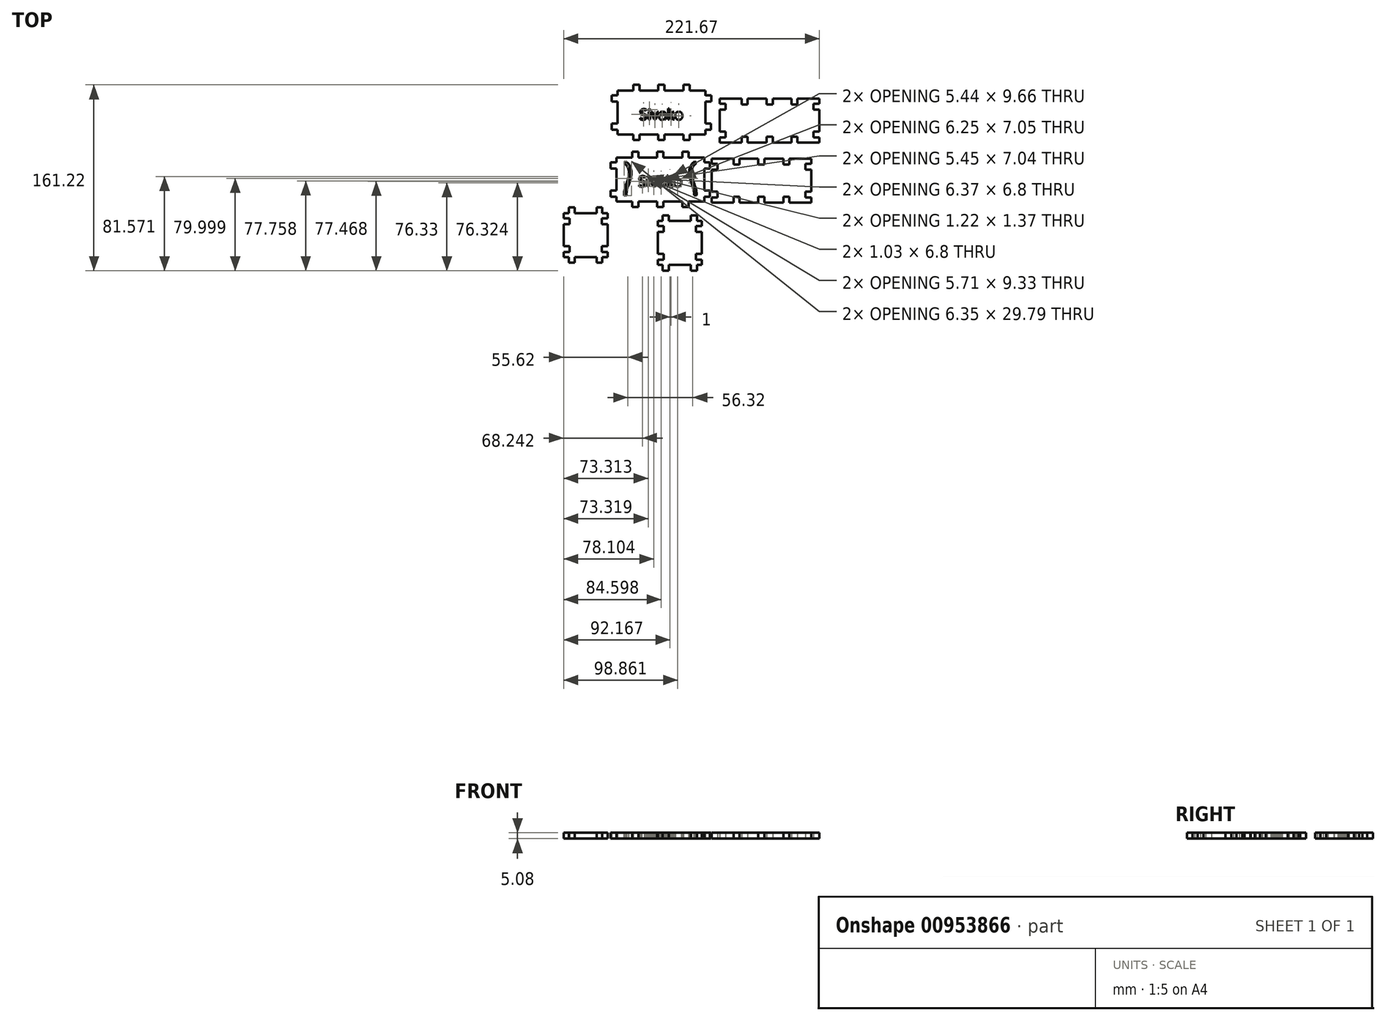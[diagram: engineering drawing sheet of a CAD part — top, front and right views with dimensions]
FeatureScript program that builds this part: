
annotation { "Feature Type Name" : "Feature", "Feature Type Description" : "" }
export const myFeature = defineFeature(function(context is Context, id is Id, definition is map)
    precondition{}
    {
        {
            var Q0;
            Q0=qCreatedBy(makeId("Top.planeOp"),FACE);
            var sketch = newSketch(context, id + "F0", { "sketchPlane" : qUnion([Q0])});
            skLineSegment(sketch, "E0.top", {"start": v(-38.1, -19.05) * mm, "end": v(38.1, -19.05) * mm});
            skLineSegment(sketch, "E0.right", {"start": v(38.1, 19.05) * mm, "end": v(38.1, -19.05) * mm});
            skPoint(sketch, "E0.middle", {"position": v(0, 0) * mm});
            skLineSegment(sketch, "E1", {"start": v(-38.1, 19.05) * mm, "end": v(-38.1, 0) * mm});
            skLineSegment(sketch, "E2", {"start": v(-38.1, 0) * mm, "end": v(-38.1, -19.05) * mm});
            skLineSegment(sketch, "E3", {"start": v(0, 19.05) * mm, "end": v(38.1, 19.05) * mm});
            skLineSegment(sketch, "E4", {"start": v(38.1, 9.52) * mm, "end": v(38.1, 9.52) * mm});
            skLineSegment(sketch, "E5.MirrorCS", {"start": v(38.1, -19.05) * mm, "end": v(38.1, 19.05) * mm});
            skLineSegment(sketch, "E6", {"start": v(38.1, -9.52) * mm, "end": v(38.1, -9.52) * mm});
            skLineSegment(sketch, "E7", {"start": v(38.1, -14.61) * mm, "end": v(38.1, -14.61) * mm});
            skLineSegment(sketch, "E8", {"start": v(-38.1, -14.61) * mm, "end": v(-38.1, -14.61) * mm});
            skLineSegment(sketch, "E9", {"start": v(-38.1, -9.52) * mm, "end": v(-38.1, -9.52) * mm});
            skLineSegment(sketch, "E10", {"start": v(-38.23, 9.65) * mm, "end": v(-38.23, 9.65) * mm});
            skLineSegment(sketch, "E11", {"start": v(-38.1, 9.53) * mm, "end": v(-43.05, 9.53) * mm});
            skLineSegment(sketch, "E12", {"start": v(-43.05, 9.53) * mm, "end": v(-43.05, 14.93) * mm});
            skLineSegment(sketch, "E13", {"start": v(-43.05, 14.93) * mm, "end": v(-38.1, 14.93) * mm});
            skLineSegment(sketch, "E14.MirrorCS", {"start": v(-38.1, -9.52) * mm, "end": v(-43.05, -9.52) * mm});
            skLineSegment(sketch, "E15.MirrorCS", {"start": v(-43.05, -9.52) * mm, "end": v(-43.05, -14.92) * mm});
            skLineSegment(sketch, "E16.MirrorCS", {"start": v(-43.05, -14.92) * mm, "end": v(-38.1, -14.92) * mm});
            skLineSegment(sketch, "E17", {"start": v(-38.1, -14.92) * mm, "end": v(-38.1, -14.92) * mm});
            skLineSegment(sketch, "E18.MirrorCS", {"start": v(43.05, 9.52) * mm, "end": v(43.05, 14.92) * mm});
            skLineSegment(sketch, "E19.MirrorCS", {"start": v(43.05, 14.92) * mm, "end": v(38.1, 14.92) * mm});
            skLineSegment(sketch, "E20.MirrorCS", {"start": v(38.1, 9.52) * mm, "end": v(43.05, 9.52) * mm});
            skLineSegment(sketch, "E21.MirrorCS", {"start": v(38.1, -9.52) * mm, "end": v(43.05, -9.52) * mm});
            skLineSegment(sketch, "E22.MirrorCS", {"start": v(43.05, -14.92) * mm, "end": v(38.1, -14.92) * mm});
            skLineSegment(sketch, "E23.MirrorCS", {"start": v(43.05, -9.52) * mm, "end": v(43.05, -14.92) * mm});
            skLineSegment(sketch, "E24", {"start": v(-19.05, 19.05) * mm, "end": v(-19.05, 24) * mm});
            skLineSegment(sketch, "E25", {"start": v(-19.05, 24) * mm, "end": v(-24.45, 24) * mm});
            skLineSegment(sketch, "E26", {"start": v(-24.45, 24) * mm, "end": v(-24.45, 19.05) * mm});
            skLineSegment(sketch, "E27.MirrorCS", {"start": v(19.05, 19.05) * mm, "end": v(19.05, 24) * mm});
            skLineSegment(sketch, "E28.MirrorCS", {"start": v(19.05, 24) * mm, "end": v(24.45, 24) * mm});
            skLineSegment(sketch, "E29.MirrorCS", {"start": v(24.45, 24) * mm, "end": v(24.45, 19.05) * mm});
            skLineSegment(sketch, "E30.MirrorCS", {"start": v(-19.05, -19.05) * mm, "end": v(-19.05, -24) * mm});
            skLineSegment(sketch, "E31.MirrorCS", {"start": v(-24.45, -24) * mm, "end": v(-24.45, -19.05) * mm});
            skLineSegment(sketch, "E32.MirrorCS", {"start": v(-19.05, -24) * mm, "end": v(-24.45, -24) * mm});
            skLineSegment(sketch, "E33.MirrorCS", {"start": v(19.05, -19.05) * mm, "end": v(19.05, -24) * mm});
            skLineSegment(sketch, "E34.MirrorCS", {"start": v(19.05, -24) * mm, "end": v(24.45, -24) * mm});
            skLineSegment(sketch, "E35.MirrorCS", {"start": v(24.45, -24) * mm, "end": v(24.45, -19.05) * mm});
            skText(sketch, "E36", { "text": "Sivako", "fontName": "OpenSans-Regular.ttf"});
            skPoint(sketch, "E36.firstSnap0", {"position": v(-19.05, 9.53) * mm});
            skPoint(sketch, "E36.secondSnap0", {"position": v(19.05, -9.52) * mm});
            skLineSegment(sketch, "E37.top", {"start": v(-37.1, 39.01) * mm, "end": v(39.1, 39.01) * mm});
            skLineSegment(sketch, "E37.right", {"start": v(39.1, 77.11) * mm, "end": v(39.1, 39.01) * mm});
            skPoint(sketch, "E37.middle", {"position": v(1, 58.06) * mm});
            skLineSegment(sketch, "E38", {"start": v(-37.1, 77.11) * mm, "end": v(-37.1, 58.07) * mm});
            skLineSegment(sketch, "E39", {"start": v(-37.1, 58.07) * mm, "end": v(-37.1, 39.01) * mm});
            skLineSegment(sketch, "E40", {"start": v(-37.1, 77.11) * mm, "end": v(1, 77.11) * mm});
            skLineSegment(sketch, "E41", {"start": v(1, 77.11) * mm, "end": v(39.1, 77.11) * mm});
            skLineSegment(sketch, "E42", {"start": v(39.1, 72.68) * mm, "end": v(39.1, 72.68) * mm});
            skLineSegment(sketch, "E43", {"start": v(39.1, 67.59) * mm, "end": v(39.1, 67.59) * mm});
            skLineSegment(sketch, "E44.MirrorCS", {"start": v(39.1, 39.01) * mm, "end": v(39.1, 77.11) * mm});
            skLineSegment(sketch, "E45", {"start": v(39.1, 48.54) * mm, "end": v(39.1, 48.54) * mm});
            skLineSegment(sketch, "E46", {"start": v(39.1, 43.45) * mm, "end": v(39.1, 43.45) * mm});
            skLineSegment(sketch, "E47", {"start": v(-37.1, 43.45) * mm, "end": v(-37.1, 43.45) * mm});
            skLineSegment(sketch, "E48", {"start": v(-37.1, 48.54) * mm, "end": v(-37.1, 48.54) * mm});
            skLineSegment(sketch, "E49", {"start": v(-37.23, 67.72) * mm, "end": v(-37.23, 67.72) * mm});
            skLineSegment(sketch, "E50", {"start": v(-37.1, 67.59) * mm, "end": v(-42.05, 67.59) * mm});
            skLineSegment(sketch, "E51", {"start": v(-42.05, 67.59) * mm, "end": v(-42.05, 72.99) * mm});
            skLineSegment(sketch, "E52", {"start": v(-42.05, 72.99) * mm, "end": v(-37.1, 72.99) * mm});
            skLineSegment(sketch, "E53.MirrorCS", {"start": v(-37.1, 48.54) * mm, "end": v(-42.06, 48.54) * mm});
            skLineSegment(sketch, "E54.MirrorCS", {"start": v(-42.06, 48.54) * mm, "end": v(-42.06, 43.14) * mm});
            skLineSegment(sketch, "E55.MirrorCS", {"start": v(-42.06, 43.14) * mm, "end": v(-37.1, 43.14) * mm});
            skLineSegment(sketch, "E56", {"start": v(-37.1, 43.14) * mm, "end": v(-37.1, 43.14) * mm});
            skLineSegment(sketch, "E57.MirrorCS", {"start": v(44.05, 67.59) * mm, "end": v(44.05, 72.99) * mm});
            skLineSegment(sketch, "E58.MirrorCS", {"start": v(44.05, 72.99) * mm, "end": v(39.1, 72.99) * mm});
            skLineSegment(sketch, "E59.MirrorCS", {"start": v(39.1, 67.59) * mm, "end": v(44.05, 67.59) * mm});
            skLineSegment(sketch, "E60.MirrorCS", {"start": v(39.1, 48.54) * mm, "end": v(44.05, 48.54) * mm});
            skLineSegment(sketch, "E61.MirrorCS", {"start": v(44.05, 43.14) * mm, "end": v(39.1, 43.14) * mm});
            skLineSegment(sketch, "E62.MirrorCS", {"start": v(44.05, 48.54) * mm, "end": v(44.05, 43.14) * mm});
            skLineSegment(sketch, "E63", {"start": v(-18.05, 77.11) * mm, "end": v(-18.05, 82.07) * mm});
            skLineSegment(sketch, "E64", {"start": v(-18.05, 82.07) * mm, "end": v(-23.45, 82.07) * mm});
            skLineSegment(sketch, "E65", {"start": v(-23.45, 82.07) * mm, "end": v(-23.45, 77.11) * mm});
            skLineSegment(sketch, "E66.MirrorCS", {"start": v(20.05, 77.11) * mm, "end": v(20.05, 82.06) * mm});
            skLineSegment(sketch, "E67.MirrorCS", {"start": v(20.05, 82.06) * mm, "end": v(25.45, 82.06) * mm});
            skLineSegment(sketch, "E68.MirrorCS", {"start": v(25.45, 82.06) * mm, "end": v(25.45, 77.11) * mm});
            skLineSegment(sketch, "E69.MirrorCS", {"start": v(-18.05, 39.02) * mm, "end": v(-18.05, 34.06) * mm});
            skLineSegment(sketch, "E70.MirrorCS", {"start": v(-23.45, 34.06) * mm, "end": v(-23.45, 39.02) * mm});
            skLineSegment(sketch, "E71.MirrorCS", {"start": v(-18.05, 34.06) * mm, "end": v(-23.45, 34.06) * mm});
            skLineSegment(sketch, "E72.MirrorCS", {"start": v(20.05, 39.02) * mm, "end": v(20.05, 34.06) * mm});
            skLineSegment(sketch, "E73.MirrorCS", {"start": v(20.05, 34.06) * mm, "end": v(25.45, 34.06) * mm});
            skLineSegment(sketch, "E74.MirrorCS", {"start": v(25.45, 34.06) * mm, "end": v(25.45, 39.02) * mm});
            skText(sketch, "E75", { "text": "Sivako", "fontName": "OpenSans-Regular.ttf"});
            skPoint(sketch, "E75.firstSnap0", {"position": v(-18.05, 67.59) * mm});
            skPoint(sketch, "E75.secondSnap0", {"position": v(20.05, 48.54) * mm});
            skLineSegment(sketch, "E76", {"start": v(0, 19.05) * mm, "end": v(-2.7, 19.05) * mm});
            skLineSegment(sketch, "E77", {"start": v(-2.7, 19.05) * mm, "end": v(2.7, 19.05) * mm});
            skLineSegment(sketch, "E78", {"start": v(2.7, 19.05) * mm, "end": v(2.7, 24) * mm});
            skLineSegment(sketch, "E79", {"start": v(2.7, 24) * mm, "end": v(-2.7, 24) * mm});
            skLineSegment(sketch, "E80", {"start": v(-2.7, 24) * mm, "end": v(-2.7, 19.05) * mm});
            skLineSegment(sketch, "E81.MirrorCS", {"start": v(-2.7, -24) * mm, "end": v(-2.7, -19.05) * mm});
            skLineSegment(sketch, "E82.MirrorCS", {"start": v(2.7, -24) * mm, "end": v(-2.7, -24) * mm});
            skLineSegment(sketch, "E83.MirrorCS", {"start": v(2.7, -19.05) * mm, "end": v(2.7, -24) * mm});
            skLineSegment(sketch, "E84", {"start": v(1, 39.01) * mm, "end": v(-1.7, 39.01) * mm});
            skLineSegment(sketch, "E85", {"start": v(1, 39.01) * mm, "end": v(3.7, 39.01) * mm});
            skLineSegment(sketch, "E86", {"start": v(3.7, 39.01) * mm, "end": v(3.7, 34.06) * mm});
            skLineSegment(sketch, "E87", {"start": v(3.7, 34.06) * mm, "end": v(-1.7, 34.06) * mm});
            skLineSegment(sketch, "E88", {"start": v(-1.7, 34.06) * mm, "end": v(-1.7, 39.01) * mm});
            skLineSegment(sketch, "E89.MirrorCS", {"start": v(3.7, 77.12) * mm, "end": v(3.7, 82.07) * mm});
            skLineSegment(sketch, "E90.MirrorCS", {"start": v(3.7, 82.07) * mm, "end": v(-1.7, 82.07) * mm});
            skLineSegment(sketch, "E91.MirrorCS", {"start": v(-1.7, 82.07) * mm, "end": v(-1.7, 77.12) * mm});
            skLineSegment(sketch, "E92", {"start": v(-1.7, 77.12) * mm, "end": v(-1.7, 77.11) * mm});
            skLineSegment(sketch, "E93", {"start": v(3.7, 77.12) * mm, "end": v(3.7, 77.11) * mm});
            skLineSegment(sketch, "E94", {"start": v(0, 2.94) * mm, "end": v(0, 19.05) * mm, "construction": true});
            skLineSegment(sketch, "E95.MirrorCS", {"start": v(28.77, -19.05) * mm, "end": v(28.77, -19.05) * mm});
            skLineSegment(sketch, "E96", {"start": v(-24.45, 19.05) * mm, "end": v(-38.1, 19.05) * mm});
            skLineSegment(sketch, "E97", {"start": v(-20, 19.05) * mm, "end": v(-2.7, 19.05) * mm});
            skLineSegment(sketch, "E98.MirrorCS", {"start": v(31.28, 19.05) * mm, "end": v(31.28, 14.05) * mm});
            skFitSpline(sketch, "E99", {"points": [v(-31.27, 14.05) * mm, v(-31.28, -14.04) * mm], "startDerivative": vector(30.27, -22.26) * mm, "endDerivative": vector(4.94, -25.33) * mm});
            skFitSpline(sketch, "E100.0", {"points": [v(-30.03, 15.74) * mm, v(-29.3, 15.2) * mm, v(-28.02, 14.07) * mm, v(-26.57, 12.18) * mm, v(-25.61, 10.13) * mm, v(-25.1, 8.02) * mm, v(-24.99, 5.92) * mm, v(-25.22, 3.15) * mm, v(-26.03, -0.23) * mm, v(-27.36, -4.12) * mm, v(-28.4, -7.17) * mm, v(-29, -9.43) * mm, v(-29.28, -11) * mm, v(-29.37, -12.42) * mm, v(-29.29, -13.25) * mm, v(-29.21, -13.64) * mm]});
            skLineSegment(sketch, "E101", {"start": v(-31.28, -14.04) * mm, "end": v(-29.21, -13.64) * mm});
            skLineSegment(sketch, "E102", {"start": v(-31.27, 14.05) * mm, "end": v(-30.03, 15.74) * mm});
            skPoint(sketch, "E103.start.orphan", {"position": v(-31.27, 19.05) * mm});
            skPoint(sketch, "E104.MirrorCS.start.orphan", {"position": v(-31.28, -19.04) * mm});
            skPoint(sketch, "E105.end.orphan", {"position": v(-28.77, -19.05) * mm});
            skPoint(sketch, "E105.start.orphan", {"position": v(-29.46, -18.35) * mm});
            skPoint(sketch, "E106.MirrorCS.end.orphan", {"position": v(31.28, -14.04) * mm});
            skPoint(sketch, "E106.MirrorCS.start.orphan", {"position": v(31.28, -19.04) * mm});
            skPoint(sketch, "E107.orphan", {"position": v(29.46, -18.35) * mm});
            skPoint(sketch, "E108.MirrorCS.end.orphan", {"position": v(31.28, 14.05) * mm});
            skPoint(sketch, "E108.MirrorCS.start.orphan", {"position": v(31.28, 19.05) * mm});
            skFitSpline(sketch, "E109.MirrorCS", {"points": [v(31.28, 14.05) * mm, v(31.27, -14.05) * mm], "startDerivative": vector(-30.27, -22.26) * mm, "endDerivative": vector(-4.94, -25.33) * mm});
            skFitSpline(sketch, "E110.0", {"points": [v(30.03, 15.74) * mm, v(29.3, 15.2) * mm, v(28.02, 14.07) * mm, v(26.57, 12.17) * mm, v(25.61, 10.13) * mm, v(25.1, 8.02) * mm, v(24.99, 5.91) * mm, v(25.22, 3.14) * mm, v(26.03, -0.23) * mm, v(27.36, -4.12) * mm, v(28.4, -7.18) * mm, v(29, -9.43) * mm, v(29.28, -11) * mm, v(29.37, -12.42) * mm, v(29.29, -13.26) * mm, v(29.21, -13.65) * mm]});
            skLineSegment(sketch, "E111.MirrorCS", {"start": v(31.27, -14.05) * mm, "end": v(29.21, -13.65) * mm});
            skLineSegment(sketch, "E112.MirrorCS", {"start": v(31.28, 14.05) * mm, "end": v(30.03, 15.74) * mm});
            skLineSegment(sketch, "E113", {"start": v(38.1, 14.92) * mm, "end": v(38.1, 14.92) * mm});
            const initialGuessF0  = {"E36": [-0.01905, -0.00622, 1, 0, 0.00915], "E75": [-0.01805, 0.05184, 1, 0, 0.00915]};
            skSetInitialGuess(sketch, initialGuessF0);
            skSolve(sketch);
        }
        {
            var Q0;
            Q0=qSketchRegion(id+"F0",true);
            var Q1;
            {var subQ6=sQuery(id+"F0.wireOp",EDGE,"E0.top");Q1=makeQuery(id+"F0.imprint","IMPRINT",FACE,{"disambiguationData":[TD([[makeQuery(id+"F0.imprint","IMPRINT",EDGE,{"derivedFrom":subQ6}),1.0]])]});}
            var Q2;
            {var subQ0=sQuery(id+"F0.wireOp",EDGE,"E36.sketch_text.stroke-40");Q2=makeQuery(id+"F0.imprint","IMPRINT",FACE,{"disambiguationData":[TD([[makeQuery(id+"F0.imprint","IMPRINT",EDGE,{"derivedFrom":subQ0}),1.0]])]});}
            var Q3;
            {var subQ0=sQuery(id+"F0.wireOp",EDGE,"E36.sketch_text.stroke-54");Q3=makeQuery(id+"F0.imprint","IMPRINT",FACE,{"disambiguationData":[TD([[makeQuery(id+"F0.imprint","IMPRINT",EDGE,{"derivedFrom":subQ0}),1.0]])]});}
            extrude(context, id + "F1", {"entities" : qUnion([Q0, Q1, Q2, Q3]), "depth" : 5.08 * mm, "offsetDistance" : 25.4 * mm});
        }
        {
            var Q0;
            Q0=qCreatedBy(makeId("Top.planeOp"),FACE);
            var sketch = newSketch(context, id + "F2", { "sketchPlane" : qUnion([Q0])});
            skLineSegment(sketch, "E114.top", {"start": v(-83.78, -67.33) * mm, "end": v(-45.68, -67.33) * mm});
            skLineSegment(sketch, "E114.right", {"start": v(-45.68, -29.23) * mm, "end": v(-45.68, -67.33) * mm});
            skPoint(sketch, "E114.middle", {"position": v(-64.73, -48.28) * mm});
            skLineSegment(sketch, "E115", {"start": v(-83.78, -29.23) * mm, "end": v(-83.78, -48.28) * mm});
            skLineSegment(sketch, "E116", {"start": v(-83.78, -48.28) * mm, "end": v(-83.78, -67.33) * mm});
            skLineSegment(sketch, "E117", {"start": v(-83.78, -38.75) * mm, "end": v(-78.7, -38.75) * mm});
            skLineSegment(sketch, "E118", {"start": v(-78.7, -38.75) * mm, "end": v(-78.7, -33.67) * mm});
            skLineSegment(sketch, "E119", {"start": v(-78.7, -33.67) * mm, "end": v(-83.78, -33.67) * mm});
            skLineSegment(sketch, "E120.MirrorCS", {"start": v(-83.78, -57.8) * mm, "end": v(-78.7, -57.8) * mm});
            skLineSegment(sketch, "E121.MirrorCS", {"start": v(-78.7, -57.8) * mm, "end": v(-78.7, -62.88) * mm});
            skLineSegment(sketch, "E122.MirrorCS", {"start": v(-78.7, -62.88) * mm, "end": v(-83.78, -62.88) * mm});
            skLineSegment(sketch, "E123.MirrorCS", {"start": v(-50.76, -38.75) * mm, "end": v(-50.76, -33.67) * mm});
            skLineSegment(sketch, "E124.MirrorCS", {"start": v(-50.76, -33.67) * mm, "end": v(-45.68, -33.67) * mm});
            skLineSegment(sketch, "E125.MirrorCS", {"start": v(-45.68, -38.75) * mm, "end": v(-50.76, -38.75) * mm});
            skLineSegment(sketch, "E126.MirrorCS", {"start": v(-45.68, -57.8) * mm, "end": v(-50.76, -57.8) * mm});
            skLineSegment(sketch, "E127.MirrorCS", {"start": v(-50.76, -57.8) * mm, "end": v(-50.76, -62.88) * mm});
            skLineSegment(sketch, "E128.MirrorCS", {"start": v(-50.76, -62.88) * mm, "end": v(-45.68, -62.88) * mm});
            skLineSegment(sketch, "E129", {"start": v(-83.78, -29.23) * mm, "end": v(-64.73, -29.23) * mm});
            skLineSegment(sketch, "E130", {"start": v(-64.73, -29.23) * mm, "end": v(-45.68, -29.23) * mm});
            skLineSegment(sketch, "E131", {"start": v(-74.25, -29.23) * mm, "end": v(-74.25, -24.28) * mm});
            skLineSegment(sketch, "E132", {"start": v(-74.25, -24.28) * mm, "end": v(-79.2, -24.28) * mm});
            skLineSegment(sketch, "E133", {"start": v(-79.2, -24.28) * mm, "end": v(-79.2, -29.23) * mm});
            skLineSegment(sketch, "E134", {"start": v(-55.2, -29.23) * mm, "end": v(-55.2, -24.28) * mm});
            skLineSegment(sketch, "E135", {"start": v(-55.2, -24.28) * mm, "end": v(-50.25, -24.28) * mm});
            skLineSegment(sketch, "E136", {"start": v(-50.25, -24.28) * mm, "end": v(-50.25, -29.23) * mm});
            skLineSegment(sketch, "E137.MirrorCS", {"start": v(-74.25, -67.33) * mm, "end": v(-74.25, -72.28) * mm});
            skLineSegment(sketch, "E138.MirrorCS", {"start": v(-74.25, -72.28) * mm, "end": v(-79.2, -72.28) * mm});
            skLineSegment(sketch, "E139.MirrorCS", {"start": v(-79.2, -72.28) * mm, "end": v(-79.2, -67.33) * mm});
            skLineSegment(sketch, "E140.MirrorCS", {"start": v(-55.2, -67.33) * mm, "end": v(-55.2, -72.28) * mm});
            skLineSegment(sketch, "E141.MirrorCS", {"start": v(-55.2, -72.28) * mm, "end": v(-50.25, -72.28) * mm});
            skLineSegment(sketch, "E142.MirrorCS", {"start": v(-50.25, -72.28) * mm, "end": v(-50.25, -67.33) * mm});
            skLineSegment(sketch, "E143.top", {"start": v(-2.2, -74.2) * mm, "end": v(35.9, -74.2) * mm});
            skLineSegment(sketch, "E143.right", {"start": v(35.9, -36.1) * mm, "end": v(35.9, -74.2) * mm});
            skPoint(sketch, "E143.middle", {"position": v(16.85, -55.15) * mm});
            skLineSegment(sketch, "E144", {"start": v(-2.2, -36.1) * mm, "end": v(-2.2, -55.15) * mm});
            skLineSegment(sketch, "E145", {"start": v(-2.2, -55.15) * mm, "end": v(-2.2, -74.2) * mm});
            skLineSegment(sketch, "E146", {"start": v(-2.2, -45.62) * mm, "end": v(2.88, -45.62) * mm});
            skLineSegment(sketch, "E147", {"start": v(2.88, -45.62) * mm, "end": v(2.88, -40.54) * mm});
            skLineSegment(sketch, "E148", {"start": v(2.88, -40.54) * mm, "end": v(-2.2, -40.54) * mm});
            skLineSegment(sketch, "E149.MirrorCS", {"start": v(-2.2, -64.67) * mm, "end": v(2.88, -64.67) * mm});
            skLineSegment(sketch, "E150.MirrorCS", {"start": v(2.88, -64.67) * mm, "end": v(2.88, -69.75) * mm});
            skLineSegment(sketch, "E151.MirrorCS", {"start": v(2.88, -69.75) * mm, "end": v(-2.2, -69.75) * mm});
            skLineSegment(sketch, "E152.MirrorCS", {"start": v(30.82, -45.62) * mm, "end": v(30.82, -40.54) * mm});
            skLineSegment(sketch, "E153.MirrorCS", {"start": v(30.82, -40.54) * mm, "end": v(35.9, -40.54) * mm});
            skLineSegment(sketch, "E154.MirrorCS", {"start": v(35.9, -45.62) * mm, "end": v(30.82, -45.62) * mm});
            skLineSegment(sketch, "E155.MirrorCS", {"start": v(35.9, -64.67) * mm, "end": v(30.82, -64.67) * mm});
            skLineSegment(sketch, "E156.MirrorCS", {"start": v(30.82, -64.67) * mm, "end": v(30.82, -69.75) * mm});
            skLineSegment(sketch, "E157.MirrorCS", {"start": v(30.82, -69.75) * mm, "end": v(35.9, -69.75) * mm});
            skLineSegment(sketch, "E158", {"start": v(-2.2, -36.1) * mm, "end": v(16.85, -36.1) * mm});
            skLineSegment(sketch, "E159", {"start": v(16.85, -36.1) * mm, "end": v(35.9, -36.1) * mm});
            skLineSegment(sketch, "E160", {"start": v(7.33, -36.1) * mm, "end": v(7.33, -31.14) * mm});
            skLineSegment(sketch, "E161", {"start": v(7.33, -31.14) * mm, "end": v(1.93, -31.14) * mm});
            skLineSegment(sketch, "E162", {"start": v(1.93, -31.14) * mm, "end": v(1.93, -36.1) * mm});
            skLineSegment(sketch, "E163", {"start": v(26.38, -36.1) * mm, "end": v(26.38, -31.14) * mm});
            skLineSegment(sketch, "E164", {"start": v(26.38, -31.14) * mm, "end": v(31.78, -31.14) * mm});
            skLineSegment(sketch, "E165", {"start": v(31.78, -31.14) * mm, "end": v(31.78, -36.1) * mm});
            skLineSegment(sketch, "E166.MirrorCS", {"start": v(7.33, -74.2) * mm, "end": v(7.33, -79.15) * mm});
            skLineSegment(sketch, "E167.MirrorCS", {"start": v(7.33, -79.15) * mm, "end": v(1.93, -79.15) * mm});
            skLineSegment(sketch, "E168.MirrorCS", {"start": v(1.93, -79.15) * mm, "end": v(1.93, -74.2) * mm});
            skLineSegment(sketch, "E169.MirrorCS", {"start": v(26.38, -74.2) * mm, "end": v(26.38, -79.15) * mm});
            skLineSegment(sketch, "E170.MirrorCS", {"start": v(26.38, -79.15) * mm, "end": v(31.78, -79.15) * mm});
            skLineSegment(sketch, "E171.MirrorCS", {"start": v(31.78, -79.15) * mm, "end": v(31.78, -74.2) * mm});
            skLineSegment(sketch, "E172.top", {"start": v(44.41, -20.23) * mm, "end": v(130.77, -20.23) * mm});
            skLineSegment(sketch, "E172.right", {"start": v(130.77, 17.87) * mm, "end": v(130.77, -20.23) * mm});
            skPoint(sketch, "E172.middle", {"position": v(87.6, -1.18) * mm});
            skLineSegment(sketch, "E173", {"start": v(44.41, 17.87) * mm, "end": v(44.41, -1.18) * mm});
            skLineSegment(sketch, "E174", {"start": v(44.41, -1.18) * mm, "end": v(44.41, -20.23) * mm});
            skLineSegment(sketch, "E175", {"start": v(44.41, 17.87) * mm, "end": v(87.6, 17.87) * mm});
            skLineSegment(sketch, "E176", {"start": v(87.6, 17.87) * mm, "end": v(130.77, 17.87) * mm});
            skLineSegment(sketch, "E177", {"start": v(87.6, 17.87) * mm, "end": v(49.5, 17.87) * mm});
            skLineSegment(sketch, "E178", {"start": v(87.6, 17.87) * mm, "end": v(125.7, 17.87) * mm});
            skLineSegment(sketch, "E179", {"start": v(68.54, 17.87) * mm, "end": v(68.54, 12.8) * mm});
            skLineSegment(sketch, "E180", {"start": v(68.54, 12.8) * mm, "end": v(63.46, 12.8) * mm});
            skLineSegment(sketch, "E181", {"start": v(63.46, 12.8) * mm, "end": v(63.46, 17.87) * mm});
            skLineSegment(sketch, "E182.MirrorCS", {"start": v(106.64, 17.87) * mm, "end": v(106.64, 12.8) * mm});
            skLineSegment(sketch, "E183.MirrorCS", {"start": v(106.64, 12.8) * mm, "end": v(111.72, 12.8) * mm});
            skLineSegment(sketch, "E184.MirrorCS", {"start": v(111.72, 12.8) * mm, "end": v(111.72, 17.87) * mm});
            skLineSegment(sketch, "E185.MirrorCS", {"start": v(68.54, -15.15) * mm, "end": v(63.46, -15.15) * mm});
            skLineSegment(sketch, "E186.MirrorCS", {"start": v(63.46, -15.15) * mm, "end": v(63.46, -20.23) * mm});
            skLineSegment(sketch, "E187.MirrorCS", {"start": v(68.54, -20.23) * mm, "end": v(68.54, -15.15) * mm});
            skLineSegment(sketch, "E188.MirrorCS", {"start": v(106.64, -15.15) * mm, "end": v(111.72, -15.15) * mm});
            skLineSegment(sketch, "E189.MirrorCS", {"start": v(106.64, -20.23) * mm, "end": v(106.64, -15.15) * mm});
            skLineSegment(sketch, "E190.MirrorCS", {"start": v(111.72, -15.15) * mm, "end": v(111.72, -20.23) * mm});
            skLineSegment(sketch, "E191.MirrorCS", {"start": v(49.5, 13.43) * mm, "end": v(44.41, 13.43) * mm});
            skLineSegment(sketch, "E192.MirrorCS", {"start": v(49.5, 8.35) * mm, "end": v(49.5, 13.43) * mm});
            skLineSegment(sketch, "E193.MirrorCS", {"start": v(44.41, 8.35) * mm, "end": v(49.5, 8.35) * mm});
            skLineSegment(sketch, "E194.MirrorCS", {"start": v(49.5, -10.7) * mm, "end": v(49.5, -15.78) * mm});
            skLineSegment(sketch, "E195.MirrorCS", {"start": v(49.5, -15.78) * mm, "end": v(44.41, -15.78) * mm});
            skLineSegment(sketch, "E196.MirrorCS", {"start": v(44.41, -10.7) * mm, "end": v(49.5, -10.7) * mm});
            skLineSegment(sketch, "E197.MirrorCS", {"start": v(125.7, 8.35) * mm, "end": v(125.7, 13.43) * mm});
            skLineSegment(sketch, "E198.MirrorCS", {"start": v(125.7, 13.43) * mm, "end": v(130.77, 13.43) * mm});
            skLineSegment(sketch, "E199.MirrorCS", {"start": v(130.77, 8.35) * mm, "end": v(125.7, 8.35) * mm});
            skLineSegment(sketch, "E200.MirrorCS", {"start": v(130.77, -10.7) * mm, "end": v(125.7, -10.7) * mm});
            skLineSegment(sketch, "E201.MirrorCS", {"start": v(125.7, -10.7) * mm, "end": v(125.7, -15.78) * mm});
            skLineSegment(sketch, "E202.MirrorCS", {"start": v(125.7, -15.78) * mm, "end": v(130.77, -15.78) * mm});
            skLineSegment(sketch, "E203.top", {"start": v(51.53, 32.1) * mm, "end": v(137.89, 32.1) * mm});
            skLineSegment(sketch, "E203.right", {"start": v(137.89, 70.2) * mm, "end": v(137.89, 32.1) * mm});
            skPoint(sketch, "E203.middle", {"position": v(94.7, 51.15) * mm});
            skLineSegment(sketch, "E204", {"start": v(51.53, 70.2) * mm, "end": v(51.53, 51.15) * mm});
            skLineSegment(sketch, "E205", {"start": v(51.53, 51.15) * mm, "end": v(51.53, 32.1) * mm});
            skLineSegment(sketch, "E206", {"start": v(51.53, 70.2) * mm, "end": v(94.7, 70.2) * mm});
            skLineSegment(sketch, "E207", {"start": v(94.7, 70.2) * mm, "end": v(137.89, 70.2) * mm});
            skLineSegment(sketch, "E208", {"start": v(94.7, 70.2) * mm, "end": v(56.6, 70.2) * mm});
            skLineSegment(sketch, "E209", {"start": v(94.7, 70.2) * mm, "end": v(132.8, 70.2) * mm});
            skLineSegment(sketch, "E210", {"start": v(75.66, 70.2) * mm, "end": v(75.66, 65.12) * mm});
            skLineSegment(sketch, "E211", {"start": v(75.66, 65.12) * mm, "end": v(70.58, 65.12) * mm});
            skLineSegment(sketch, "E212", {"start": v(70.58, 65.12) * mm, "end": v(70.58, 70.2) * mm});
            skLineSegment(sketch, "E213.MirrorCS", {"start": v(113.76, 70.2) * mm, "end": v(113.76, 65.12) * mm});
            skLineSegment(sketch, "E214.MirrorCS", {"start": v(113.76, 65.12) * mm, "end": v(118.84, 65.12) * mm});
            skLineSegment(sketch, "E215.MirrorCS", {"start": v(118.84, 65.12) * mm, "end": v(118.84, 70.2) * mm});
            skLineSegment(sketch, "E216.MirrorCS", {"start": v(75.66, 37.18) * mm, "end": v(70.58, 37.18) * mm});
            skLineSegment(sketch, "E217.MirrorCS", {"start": v(70.58, 37.18) * mm, "end": v(70.58, 32.1) * mm});
            skLineSegment(sketch, "E218.MirrorCS", {"start": v(75.66, 32.1) * mm, "end": v(75.66, 37.18) * mm});
            skLineSegment(sketch, "E219.MirrorCS", {"start": v(113.76, 37.18) * mm, "end": v(118.84, 37.18) * mm});
            skLineSegment(sketch, "E220.MirrorCS", {"start": v(113.76, 32.1) * mm, "end": v(113.76, 37.18) * mm});
            skLineSegment(sketch, "E221.MirrorCS", {"start": v(118.84, 37.18) * mm, "end": v(118.84, 32.1) * mm});
            skLineSegment(sketch, "E222.MirrorCS", {"start": v(56.6, 65.76) * mm, "end": v(51.53, 65.76) * mm});
            skLineSegment(sketch, "E223.MirrorCS", {"start": v(56.6, 60.68) * mm, "end": v(56.6, 65.76) * mm});
            skLineSegment(sketch, "E224.MirrorCS", {"start": v(51.53, 60.68) * mm, "end": v(56.6, 60.68) * mm});
            skLineSegment(sketch, "E225.MirrorCS", {"start": v(56.6, 41.63) * mm, "end": v(56.6, 36.55) * mm});
            skLineSegment(sketch, "E226.MirrorCS", {"start": v(56.6, 36.55) * mm, "end": v(51.53, 36.55) * mm});
            skLineSegment(sketch, "E227.MirrorCS", {"start": v(51.53, 41.63) * mm, "end": v(56.6, 41.63) * mm});
            skLineSegment(sketch, "E228.MirrorCS", {"start": v(132.8, 60.68) * mm, "end": v(132.8, 65.76) * mm});
            skLineSegment(sketch, "E229.MirrorCS", {"start": v(132.8, 65.76) * mm, "end": v(137.89, 65.76) * mm});
            skLineSegment(sketch, "E230.MirrorCS", {"start": v(137.89, 60.68) * mm, "end": v(132.8, 60.68) * mm});
            skLineSegment(sketch, "E231.MirrorCS", {"start": v(137.89, 41.63) * mm, "end": v(132.8, 41.63) * mm});
            skLineSegment(sketch, "E232.MirrorCS", {"start": v(132.8, 41.63) * mm, "end": v(132.8, 36.55) * mm});
            skLineSegment(sketch, "E233.MirrorCS", {"start": v(132.8, 36.55) * mm, "end": v(137.89, 36.55) * mm});
            skPoint(sketch, "E234.orphan", {"position": v(130.77, -1.18) * mm});
            skLineSegment(sketch, "E235", {"start": v(87.6, 17.87) * mm, "end": v(84.9, 17.87) * mm});
            skLineSegment(sketch, "E236", {"start": v(84.9, 17.87) * mm, "end": v(90.3, 17.87) * mm});
            skLineSegment(sketch, "E237", {"start": v(90.3, 17.87) * mm, "end": v(90.3, 12.8) * mm});
            skLineSegment(sketch, "E238", {"start": v(90.3, 12.8) * mm, "end": v(84.9, 12.8) * mm});
            skLineSegment(sketch, "E239", {"start": v(84.9, 12.8) * mm, "end": v(84.9, 17.87) * mm});
            skLineSegment(sketch, "E240.MirrorCS", {"start": v(90.3, -20.23) * mm, "end": v(90.3, -15.15) * mm});
            skLineSegment(sketch, "E241.MirrorCS", {"start": v(84.9, -15.15) * mm, "end": v(84.9, -20.23) * mm});
            skLineSegment(sketch, "E242.MirrorCS", {"start": v(90.3, -15.15) * mm, "end": v(84.9, -15.15) * mm});
            skLineSegment(sketch, "E243", {"start": v(94.7, 70.2) * mm, "end": v(92, 70.2) * mm});
            skLineSegment(sketch, "E244", {"start": v(92, 70.2) * mm, "end": v(100.64, 70.2) * mm});
            skLineSegment(sketch, "E245", {"start": v(94.7, 70.2) * mm, "end": v(97.4, 70.2) * mm});
            skLineSegment(sketch, "E246", {"start": v(97.4, 70.2) * mm, "end": v(97.4, 65.12) * mm});
            skLineSegment(sketch, "E247", {"start": v(97.4, 65.12) * mm, "end": v(92, 65.12) * mm});
            skLineSegment(sketch, "E248", {"start": v(92, 65.12) * mm, "end": v(92, 70.2) * mm});
            skLineSegment(sketch, "E249.MirrorCS", {"start": v(97.4, 32.1) * mm, "end": v(97.4, 37.18) * mm});
            skLineSegment(sketch, "E250.MirrorCS", {"start": v(97.4, 37.18) * mm, "end": v(92, 37.18) * mm});
            skLineSegment(sketch, "E251.MirrorCS", {"start": v(92, 37.18) * mm, "end": v(92, 32.1) * mm});
            skSolve(sketch);
        }
        {
            var Q0;
            {var subQ3=sQuery(id+"F2.wireOp",EDGE,"E117");Q0=makeQuery(id+"F2.imprint","IMPRINT",FACE,{"disambiguationData":[TD([[makeQuery(id+"F2.imprint","IMPRINT",EDGE,{"derivedFrom":subQ3}),-1.0]])]});}
            var Q1;
            {var subQ10=sQuery(id+"F2.wireOp",EDGE,"E120.MirrorCS");Q1=makeQuery(id+"F2.imprint","IMPRINT",FACE,{"disambiguationData":[TD([[makeQuery(id+"F2.imprint","IMPRINT",EDGE,{"derivedFrom":subQ10}),1.0]])]});}
            var Q2;
            {var subQ6=sQuery(id+"F2.wireOp",EDGE,"E126.MirrorCS");Q2=makeQuery(id+"F2.imprint","IMPRINT",FACE,{"disambiguationData":[TD([[makeQuery(id+"F2.imprint","IMPRINT",EDGE,{"derivedFrom":subQ6}),-1.0]])]});}
            var Q3;
            Q3=makeQuery(id+"F2.imprint","IMPRINT",FACE,{"disambiguationData":[TD([[makeQuery(id+"F2.imprint","IMPRINT",EDGE,{"derivedFrom":sQuery(id+"F2.wireOp",EDGE,"E123.MirrorCS")}),1.0]])]});
            var Q4;
            {var subQ0=sQuery(id+"F2.wireOp",EDGE,"E140.MirrorCS");Q4=makeQuery(id+"F2.imprint","IMPRINT",FACE,{"disambiguationData":[TD([[makeQuery(id+"F2.imprint","IMPRINT",EDGE,{"derivedFrom":subQ0}),1.0]])]});}
            var Q5;
            {var subQ0=sQuery(id+"F2.wireOp",EDGE,"E137.MirrorCS");Q5=makeQuery(id+"F2.imprint","IMPRINT",FACE,{"disambiguationData":[TD([[makeQuery(id+"F2.imprint","IMPRINT",EDGE,{"derivedFrom":subQ0}),-1.0]])]});}
            var Q6;
            {var subQ0=sQuery(id+"F2.wireOp",EDGE,"E131");Q6=makeQuery(id+"F2.imprint","IMPRINT",FACE,{"disambiguationData":[TD([[makeQuery(id+"F2.imprint","IMPRINT",EDGE,{"derivedFrom":subQ0}),1.0]])]});}
            var Q7;
            {var subQ0=sQuery(id+"F2.wireOp",EDGE,"E134");Q7=makeQuery(id+"F2.imprint","IMPRINT",FACE,{"disambiguationData":[TD([[makeQuery(id+"F2.imprint","IMPRINT",EDGE,{"derivedFrom":subQ0}),-1.0]])]});}
            var Q8;
            {var subQ10=sQuery(id+"F2.wireOp",EDGE,"E149.MirrorCS");Q8=makeQuery(id+"F2.imprint","IMPRINT",FACE,{"disambiguationData":[TD([[makeQuery(id+"F2.imprint","IMPRINT",EDGE,{"derivedFrom":subQ10}),1.0]])]});}
            var Q9;
            {var subQ6=sQuery(id+"F2.wireOp",EDGE,"E155.MirrorCS");Q9=makeQuery(id+"F2.imprint","IMPRINT",FACE,{"disambiguationData":[TD([[makeQuery(id+"F2.imprint","IMPRINT",EDGE,{"derivedFrom":subQ6}),-1.0]])]});}
            var Q10;
            Q10=makeQuery(id+"F2.imprint","IMPRINT",FACE,{"disambiguationData":[TD([[makeQuery(id+"F2.imprint","IMPRINT",EDGE,{"derivedFrom":sQuery(id+"F2.wireOp",EDGE,"E152.MirrorCS")}),1.0]])]});
            var Q11;
            {var subQ3=sQuery(id+"F2.wireOp",EDGE,"E146");Q11=makeQuery(id+"F2.imprint","IMPRINT",FACE,{"disambiguationData":[TD([[makeQuery(id+"F2.imprint","IMPRINT",EDGE,{"derivedFrom":subQ3}),-1.0]])]});}
            var Q12;
            {var subQ0=sQuery(id+"F2.wireOp",EDGE,"E169.MirrorCS");Q12=makeQuery(id+"F2.imprint","IMPRINT",FACE,{"disambiguationData":[TD([[makeQuery(id+"F2.imprint","IMPRINT",EDGE,{"derivedFrom":subQ0}),1.0]])]});}
            var Q13;
            {var subQ0=sQuery(id+"F2.wireOp",EDGE,"E166.MirrorCS");Q13=makeQuery(id+"F2.imprint","IMPRINT",FACE,{"disambiguationData":[TD([[makeQuery(id+"F2.imprint","IMPRINT",EDGE,{"derivedFrom":subQ0}),-1.0]])]});}
            var Q14;
            {var subQ0=sQuery(id+"F2.wireOp",EDGE,"E160");Q14=makeQuery(id+"F2.imprint","IMPRINT",FACE,{"disambiguationData":[TD([[makeQuery(id+"F2.imprint","IMPRINT",EDGE,{"derivedFrom":subQ0}),1.0]])]});}
            var Q15;
            {var subQ0=sQuery(id+"F2.wireOp",EDGE,"E163");Q15=makeQuery(id+"F2.imprint","IMPRINT",FACE,{"disambiguationData":[TD([[makeQuery(id+"F2.imprint","IMPRINT",EDGE,{"derivedFrom":subQ0}),-1.0]])]});}
            extrude(context, id + "F3", {"entities" : qUnion([Q0, Q1, Q2, Q3, Q4, Q5, Q6, Q7, Q8, Q9, Q10, Q11, Q12, Q13, Q14, Q15]), "depth" : 5.08 * mm, "offsetDistance" : 25.4 * mm});
        }
        {
            var Q0;
            {var subQ3=sQuery(id+"F2.wireOp",EDGE,"78740de0-593b-4ee4-b9a7-870c1f821584");Q0=makeQuery(id+"F2.imprint","IMPRINT",FACE,{"disambiguationData":[TD([[makeQuery(id+"F2.imprint","IMPRINT",EDGE,{"derivedFrom":subQ3}),1.0]])]});}
            var Q1;
            Q1=makeQuery(id+"F2.imprint","IMPRINT",FACE,{"disambiguationData":[TD([[makeQuery(id+"F2.imprint","IMPRINT",EDGE,{"derivedFrom":sQuery(id+"F2.wireOp",EDGE,"E185.MirrorCS")}),-1.0]])]});
            var Q2;
            {var subQ2=sQuery(id+"F2.wireOp",EDGE,"78740de0-593b-4ee4-b9a7-870c1f821584");Q2=makeQuery(id+"F2.imprint","IMPRINT",FACE,{"disambiguationData":[TD([[makeQuery(id+"F2.imprint","IMPRINT",EDGE,{"derivedFrom":subQ2}),-1.0]])]});}
            var Q3;
            Q3=makeQuery(id+"F2.imprint","IMPRINT",FACE,{"disambiguationData":[TD([[makeQuery(id+"F2.imprint","IMPRINT",EDGE,{"derivedFrom":sQuery(id+"F2.wireOp",EDGE,"E216.MirrorCS")}),-1.0]])]});
            var Q4;
            {var subQ2=sQuery(id+"F2.wireOp",EDGE,"E207");Q4=makeQuery(id+"F2.imprint","IMPRINT",FACE,{"disambiguationData":[TD([[makeQuery(id+"F2.imprint","IMPRINT",EDGE,{"derivedFrom":subQ2}),-1.0]])]});}
            var Q5;
            {var subQ3=sQuery(id+"F2.wireOp",EDGE,"E206");Q5=makeQuery(id+"F2.imprint","IMPRINT",FACE,{"disambiguationData":[TD([[makeQuery(id+"F2.imprint","IMPRINT",EDGE,{"derivedFrom":subQ3}),-1.0]])]});}
            extrude(context, id + "F4", {"entities" : qUnion([Q0, Q1, Q2, Q3, Q4, Q5]), "depth" : 5.08 * mm, "offsetDistance" : 25.4 * mm});
        }
    });
